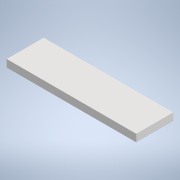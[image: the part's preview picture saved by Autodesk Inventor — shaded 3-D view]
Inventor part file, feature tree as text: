
AUTODESK INVENTOR PART (.ipt)
format: ipt  version: 2020.2 (Build 242310000, 310)  size: 90,624 bytes
history: native  units: mm
features: extrude x1, sketch x1
ambient origin geometry x8: Origin, YZ Plane, XZ Plane, XY Plane, X Axis, Y Axis, Z Axis, Center Point
bodies: Solido1 (feature_tree)
feature tree (2):
  extrude  "Estrusione1"  Depth=70.0mm
  sketch  "Schizzo1"
